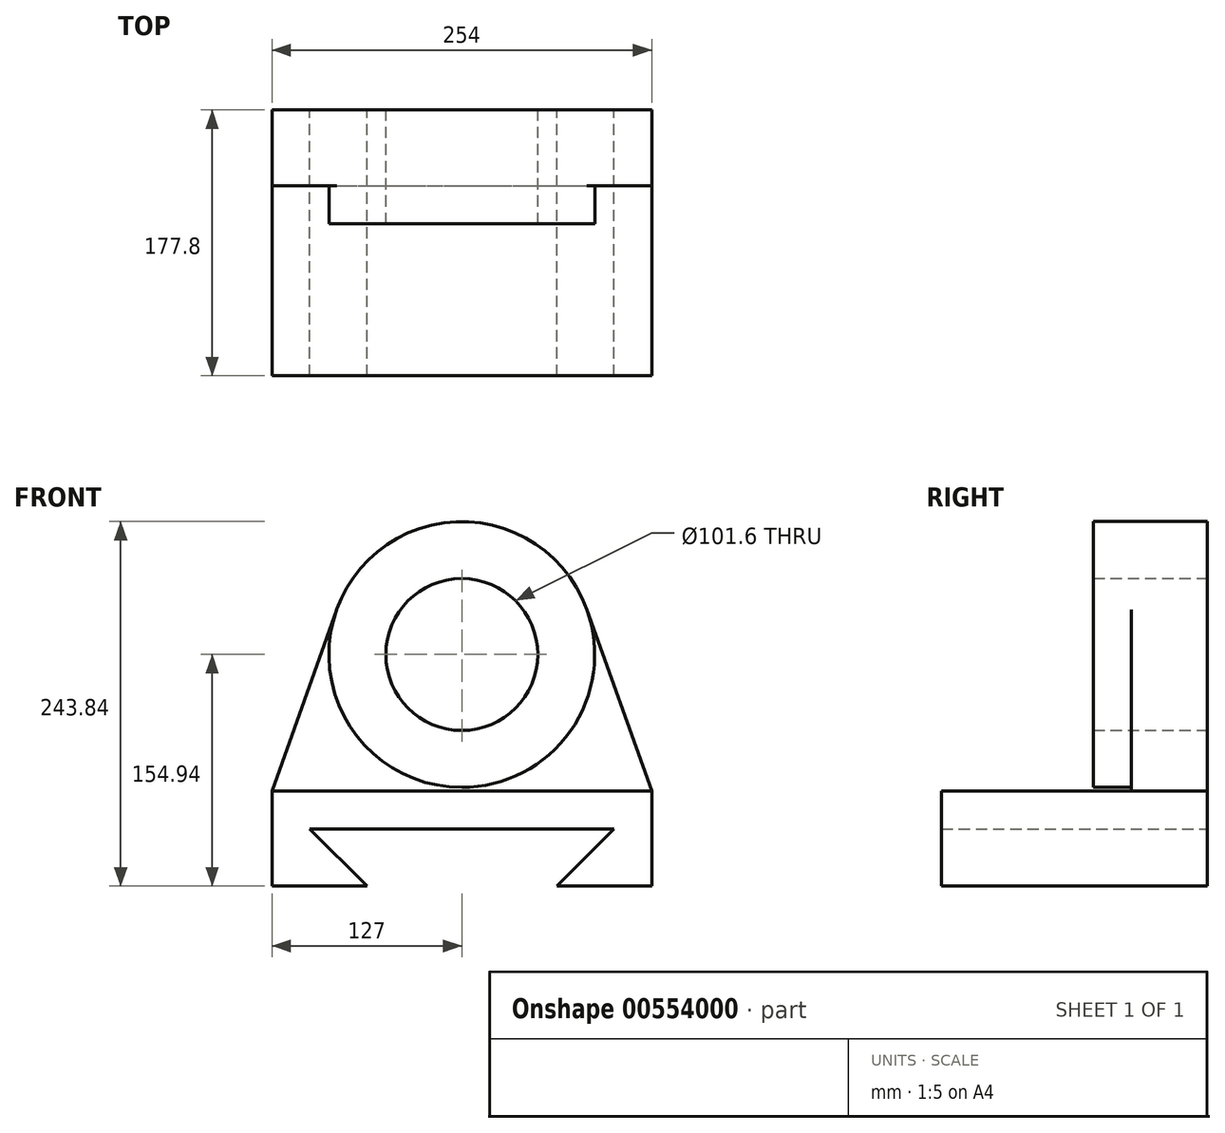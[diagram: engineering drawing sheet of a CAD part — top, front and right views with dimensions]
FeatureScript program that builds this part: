
annotation { "Feature Type Name" : "Feature", "Feature Type Description" : "" }
export const myFeature = defineFeature(function(context is Context, id is Id, definition is map)
    precondition{}
    {
        {
            var Q0;
            Q0=qCreatedBy(makeId("Front.planeOp"),FACE);
            var sketch = newSketch(context, id + "F0", { "sketchPlane" : qUnion([Q0])});
            skLineSegment(sketch, "E0", {"start": v(0, 0) * mm, "end": v(254, 0) * mm});
            skLineSegment(sketch, "E1", {"start": v(0, 0) * mm, "end": v(0, -63.5) * mm});
            skLineSegment(sketch, "E2", {"start": v(254, 0) * mm, "end": v(254, -63.5) * mm});
            skLineSegment(sketch, "E3", {"start": v(25.4, -25.4) * mm, "end": v(228.6, -25.4) * mm});
            skLineSegment(sketch, "E4", {"start": v(25.4, -25.4) * mm, "end": v(63.5, -63.5) * mm});
            skLineSegment(sketch, "E5", {"start": v(228.6, -25.4) * mm, "end": v(190.5, -63.5) * mm});
            skLineSegment(sketch, "E6", {"start": v(0, -63.5) * mm, "end": v(63.5, -63.5) * mm});
            skLineSegment(sketch, "E7", {"start": v(190.5, -63.5) * mm, "end": v(254, -63.5) * mm});
            skCircle(sketch, "E8", {"center": v(127, 91.44) * mm, "radius": 50.8 * mm});
            skCircle(sketch, "E9", {"center": v(127, 91.44) * mm, "radius": 88.9 * mm});
            skLineSegment(sketch, "E10", {"start": v(43.27, 121.3) * mm, "end": v(0, 0) * mm});
            skLineSegment(sketch, "E11", {"start": v(210.73, 121.3) * mm, "end": v(254, 0) * mm});
            skSolve(sketch);
        }
        {
            var Q0;
            Q0=makeQuery(id+"F0.imprint","IMPRINT",FACE,{"disambiguationData":[TD([[makeQuery(id+"F0.imprint","IMPRINT",EDGE,{"derivedFrom":sQuery(id+"F0.wireOp",EDGE,"E0")}),-1.0]])]});
            extrude(context, id + "F1", {"entities" : qUnion([Q0]), "depth" : 177.8 * mm, "offsetDistance" : 25.4 * mm});
        }
        {
            var Q0;
            Q0=makeQuery(id+"F0.imprint","IMPRINT",FACE,{"disambiguationData":[TD([[makeQuery(id+"F0.imprint","IMPRINT",EDGE,{"derivedFrom":sQuery(id+"F0.wireOp",EDGE,"E0")}),1.0]])]});
            var Q1;
            Q1=makeQuery(id+"F0.imprint","IMPRINT",FACE,{"disambiguationData":[TD([[makeQuery(id+"F0.imprint","IMPRINT",EDGE,{"derivedFrom":sQuery(id+"F0.wireOp",EDGE,"E8")}),-1.0]])]});
            extrude(context, id + "F2", {"entities" : qUnion([Q0, Q1]), "operationType" : NewBodyOperationType.ADD, "depth" : 50.8 * mm, "offsetDistance" : 25.4 * mm});
        }
        {
            var Q0;
            Q0=makeQuery(id+"F0.imprint","IMPRINT",FACE,{"disambiguationData":[TD([[makeQuery(id+"F0.imprint","IMPRINT",EDGE,{"derivedFrom":sQuery(id+"F0.wireOp",EDGE,"E8")}),-1.0]])]});
            extrude(context, id + "F3", {"entities" : qUnion([Q0]), "operationType" : NewBodyOperationType.ADD, "depth" : 76.2 * mm, "offsetDistance" : 25.4 * mm});
        }
    });
